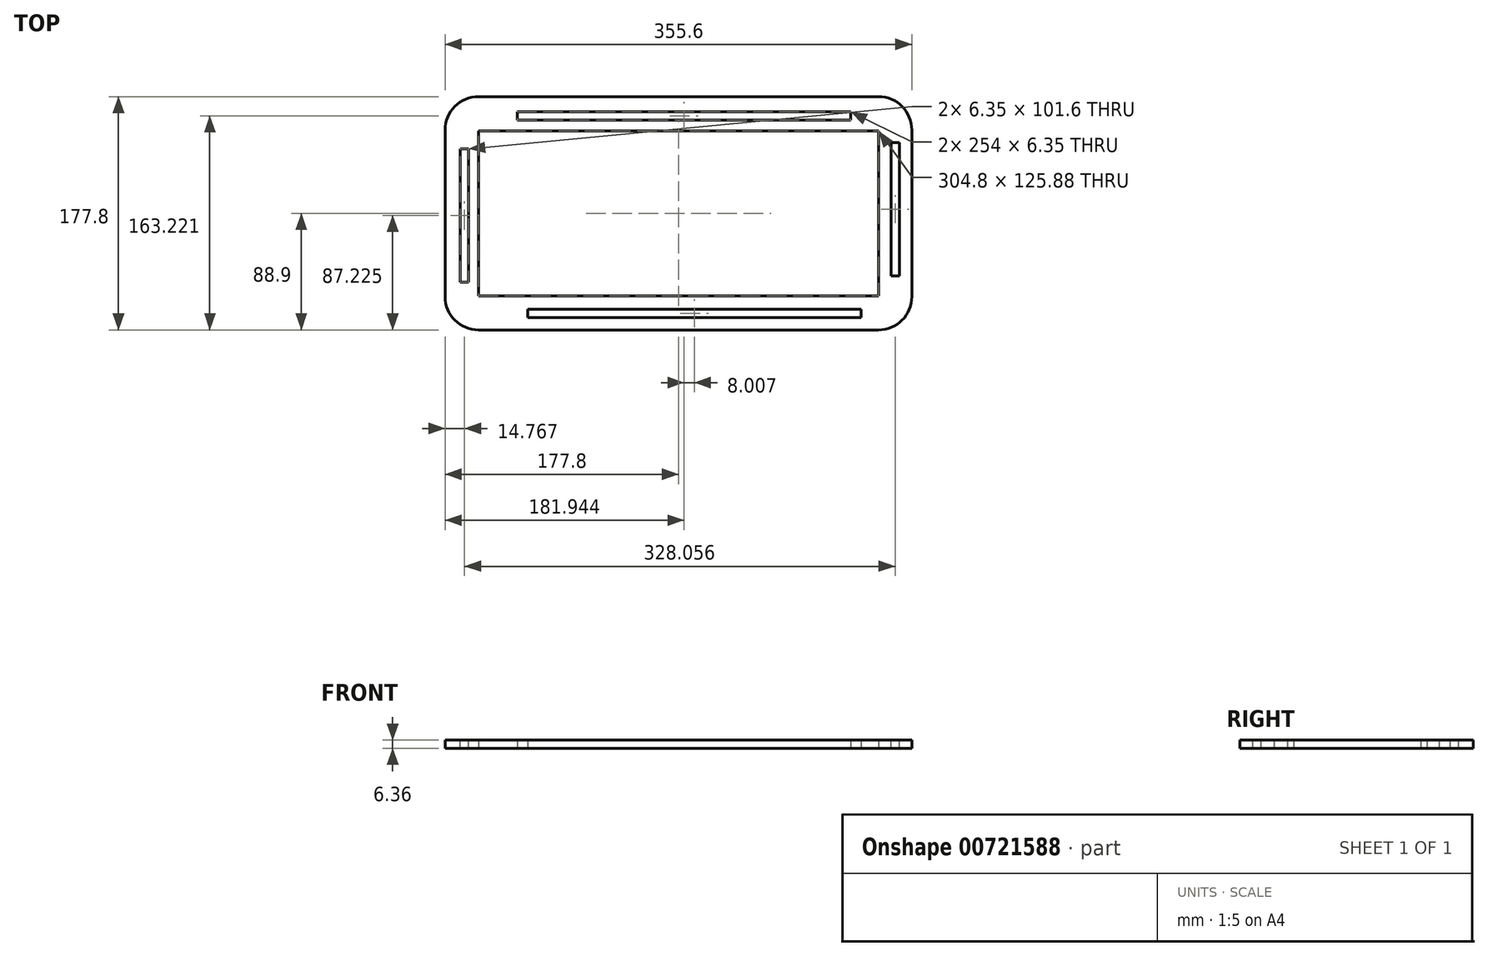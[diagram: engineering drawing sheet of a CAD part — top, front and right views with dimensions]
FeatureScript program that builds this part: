
annotation { "Feature Type Name" : "Feature", "Feature Type Description" : "" }
export const myFeature = defineFeature(function(context is Context, id is Id, definition is map)
    precondition{}
    {
        {
            var Q0;
            Q0=qCreatedBy(makeId("Top.planeOp"),FACE);
            var sketch = newSketch(context, id + "F0", { "sketchPlane" : qUnion([Q0])});
            skLineSegment(sketch, "E0.bottom", {"start": v(152.4, -62.94) * mm, "end": v(-152.4, -62.94) * mm});
            skLineSegment(sketch, "E0.top", {"start": v(152.4, 62.94) * mm, "end": v(-152.4, 62.94) * mm});
            skLineSegment(sketch, "E0.left", {"start": v(152.4, -62.94) * mm, "end": v(152.4, 62.94) * mm});
            skLineSegment(sketch, "E0.right", {"start": v(-152.4, -62.94) * mm, "end": v(-152.4, 62.94) * mm});
            skPoint(sketch, "E0.middle", {"position": v(0, 0) * mm});
            skSolve(sketch);
        }
        {
            var Q0;
            Q0=makeQuery(id+"F0.imprint","IMPRINT",FACE,{"disambiguationData":[TD([[makeQuery(id+"F0.imprint","IMPRINT",EDGE,{"derivedFrom":sQuery(id+"F0.wireOp",EDGE,"E0.bottom")}),-1.0]])]});
            extrude(context, id + "F1", {"entities" : qUnion([Q0]), "depth" : 6.35 * mm, "offsetDistance" : 25.4 * mm, "symmetric" : true});
        }
        {
            var Q0;
            Q0=qCreatedBy(makeId("Top.planeOp"),FACE);
            var sketch = newSketch(context, id + "F2", { "sketchPlane" : qUnion([Q0])});
            skLineSegment(sketch, "E1.bottom", {"start": v(177.8, -88.9) * mm, "end": v(-177.8, -88.9) * mm});
            skLineSegment(sketch, "E1.top", {"start": v(177.8, 88.9) * mm, "end": v(-177.8, 88.9) * mm});
            skLineSegment(sketch, "E1.left", {"start": v(177.8, -88.9) * mm, "end": v(177.8, 88.9) * mm});
            skLineSegment(sketch, "E1.right", {"start": v(-177.8, -88.9) * mm, "end": v(-177.8, 88.9) * mm});
            skPoint(sketch, "E1.middle", {"position": v(0, 0) * mm});
            skSolve(sketch);
        }
        {
            var Q0;
            Q0=qSketchRegion(id+"F2",true);
            extrude(context, id + "F3", {"entities" : qUnion([Q0]), "operationType" : NewBodyOperationType.ADD, "depth" : 6.35 * mm, "offsetDistance" : 25.4 * mm, "symmetric" : true});
        }
        {
            var Q0;
            Q0=qSketchRegion(id+"F0",true);
            extrude(context, id + "F4", {"entities" : qUnion([Q0]), "operationType" : NewBodyOperationType.REMOVE, "depth" : 25.4 * mm, "offsetDistance" : 25.4 * mm, "symmetric" : true});
        }
        {
            var Q0;
            Q0=makeQuery(id+"F3.opExtrude","SWEPT_EDGE",EDGE,{"disambiguationData":[OSD([sQuery(id+"F2.wireOp",EDGE,"E1.top"),sQuery(id+"F2.wireOp",EDGE,"E1.right")])]});
            fillet(context, id + "F5", {"entities" : qUnion([Q0]), "radius" : 25.4 * mm, "tangentPropagation" : true, "allowEdgeOverflow" : false});
        }
        {
            var Q0;
            Q0=makeQuery(id+"F3.opExtrude","SWEPT_EDGE",EDGE,{"disambiguationData":[OSD([sQuery(id+"F2.wireOp",EDGE,"E1.top"),sQuery(id+"F2.wireOp",EDGE,"E1.left")])]});
            fillet(context, id + "F6", {"entities" : qUnion([Q0]), "radius" : 25.4 * mm, "tangentPropagation" : true, "allowEdgeOverflow" : false});
        }
        {
            var Q0;
            Q0=makeQuery(id+"F3.opExtrude","SWEPT_EDGE",EDGE,{"disambiguationData":[OSD([sQuery(id+"F2.wireOp",EDGE,"E1.bottom"),sQuery(id+"F2.wireOp",EDGE,"E1.left")])]});
            fillet(context, id + "F7", {"entities" : qUnion([Q0]), "radius" : 25.4 * mm, "tangentPropagation" : true, "allowEdgeOverflow" : false});
        }
        {
            var Q0;
            Q0=makeQuery(id+"F3.opExtrude","SWEPT_EDGE",EDGE,{"disambiguationData":[OSD([sQuery(id+"F2.wireOp",EDGE,"E1.bottom"),sQuery(id+"F2.wireOp",EDGE,"E1.right")])]});
            fillet(context, id + "F8", {"entities" : qUnion([Q0]), "radius" : 25.4 * mm, "tangentPropagation" : true, "allowEdgeOverflow" : false});
        }
        {
            var Q0;
            Q0=makeQuery(id+"F2.imprint","IMPRINT",FACE,{"disambiguationData":[TD([[makeQuery(id+"F2.imprint","IMPRINT",EDGE,{"derivedFrom":sQuery(id+"F2.wireOp",EDGE,"E1.bottom")}),-1.0]])]});
            var sketch = newSketch(context, id + "F9", { "sketchPlane" : qUnion([Q0])});
            skLineSegment(sketch, "E2.bottom", {"start": v(-122.86, 77.5) * mm, "end": v(131.14, 77.5) * mm});
            skLineSegment(sketch, "E2.top", {"start": v(-122.86, 71.15) * mm, "end": v(131.14, 71.15) * mm});
            skLineSegment(sketch, "E2.left", {"start": v(-122.86, 77.5) * mm, "end": v(-122.86, 71.15) * mm});
            skLineSegment(sketch, "E2.right", {"start": v(131.14, 77.5) * mm, "end": v(131.14, 71.15) * mm});
            skSolve(sketch);
        }
        {
            var Q0;
            Q0=makeQuery(id+"F9.imprint","IMPRINT",FACE,{"disambiguationData":[TD([[makeQuery(id+"F9.imprint","IMPRINT",EDGE,{"derivedFrom":sQuery(id+"F9.wireOp",EDGE,"E2.bottom")}),-1.0]])]});
            extrude(context, id + "F10", {"entities" : qUnion([Q0]), "operationType" : NewBodyOperationType.REMOVE, "depth" : 25.4 * mm, "offsetDistance" : 25.4 * mm, "symmetric" : true});
        }
        {
            var Q0;
            Q0=makeQuery(id+"F2.imprint","IMPRINT",FACE,{"disambiguationData":[TD([[makeQuery(id+"F2.imprint","IMPRINT",EDGE,{"derivedFrom":sQuery(id+"F2.wireOp",EDGE,"E1.bottom")}),-1.0]])]});
            var sketch = newSketch(context, id + "F11", { "sketchPlane" : qUnion([Q0])});
            skLineSegment(sketch, "E3.bottom", {"start": v(-114.85, -72.97) * mm, "end": v(139.15, -72.97) * mm});
            skLineSegment(sketch, "E3.top", {"start": v(-114.85, -79.32) * mm, "end": v(139.15, -79.32) * mm});
            skLineSegment(sketch, "E3.left", {"start": v(-114.85, -72.97) * mm, "end": v(-114.85, -79.32) * mm});
            skLineSegment(sketch, "E3.right", {"start": v(139.15, -72.97) * mm, "end": v(139.15, -79.32) * mm});
            skSolve(sketch);
        }
        {
            var Q0;
            Q0 = qSketchRegion(id + "F11", true);
            extrude(context, id + "F12", {"entities" : qUnion([Q0]), "operationType" : NewBodyOperationType.REMOVE, "depth" : 25.4 * mm, "offsetDistance" : 25.4 * mm, "symmetric" : true});
        }
        {
            var Q0;
            Q0=makeQuery(id+"F2.imprint","IMPRINT",FACE,{"disambiguationData":[TD([[makeQuery(id+"F2.imprint","IMPRINT",EDGE,{"derivedFrom":sQuery(id+"F2.wireOp",EDGE,"E1.bottom")}),-1.0]])]});
            var sketch = newSketch(context, id + "F13", { "sketchPlane" : qUnion([Q0])});
            skLineSegment(sketch, "E4.bottom", {"start": v(-166.2, 49.12) * mm, "end": v(-159.86, 49.12) * mm});
            skLineSegment(sketch, "E4.top", {"start": v(-166.2, -52.48) * mm, "end": v(-159.86, -52.48) * mm});
            skLineSegment(sketch, "E4.left", {"start": v(-166.2, 49.12) * mm, "end": v(-166.2, -52.48) * mm});
            skLineSegment(sketch, "E4.right", {"start": v(-159.86, 49.12) * mm, "end": v(-159.86, -52.48) * mm});
            skSolve(sketch);
        }
        {
            var Q0;
            Q0 = qSketchRegion(id + "F13", true);
            extrude(context, id + "F14", {"entities" : qUnion([Q0]), "operationType" : NewBodyOperationType.REMOVE, "oppositeDirection" : true, "depth" : 25.4 * mm, "offsetDistance" : 25.4 * mm, "symmetric" : true});
        }
        {
            var Q0;
            Q0=makeQuery(id+"F2.imprint","IMPRINT",FACE,{"disambiguationData":[TD([[makeQuery(id+"F2.imprint","IMPRINT",EDGE,{"derivedFrom":sQuery(id+"F2.wireOp",EDGE,"E1.bottom")}),-1.0]])]});
            var sketch = newSketch(context, id + "F15", { "sketchPlane" : qUnion([Q0])});
            skLineSegment(sketch, "E5.bottom", {"start": v(161.85, 54) * mm, "end": v(168.2, 54) * mm});
            skLineSegment(sketch, "E5.top", {"start": v(161.85, -47.6) * mm, "end": v(168.2, -47.6) * mm});
            skLineSegment(sketch, "E5.left", {"start": v(161.85, 54) * mm, "end": v(161.85, -47.6) * mm});
            skLineSegment(sketch, "E5.right", {"start": v(168.2, 54) * mm, "end": v(168.2, -47.6) * mm});
            skSolve(sketch);
        }
        {
            var Q0;
            Q0 = qSketchRegion(id + "F15", true);
            extrude(context, id + "F16", {"entities" : qUnion([Q0]), "operationType" : NewBodyOperationType.REMOVE, "oppositeDirection" : true, "depth" : 25.4 * mm, "offsetDistance" : 25.4 * mm, "symmetric" : true});
        }
    });
